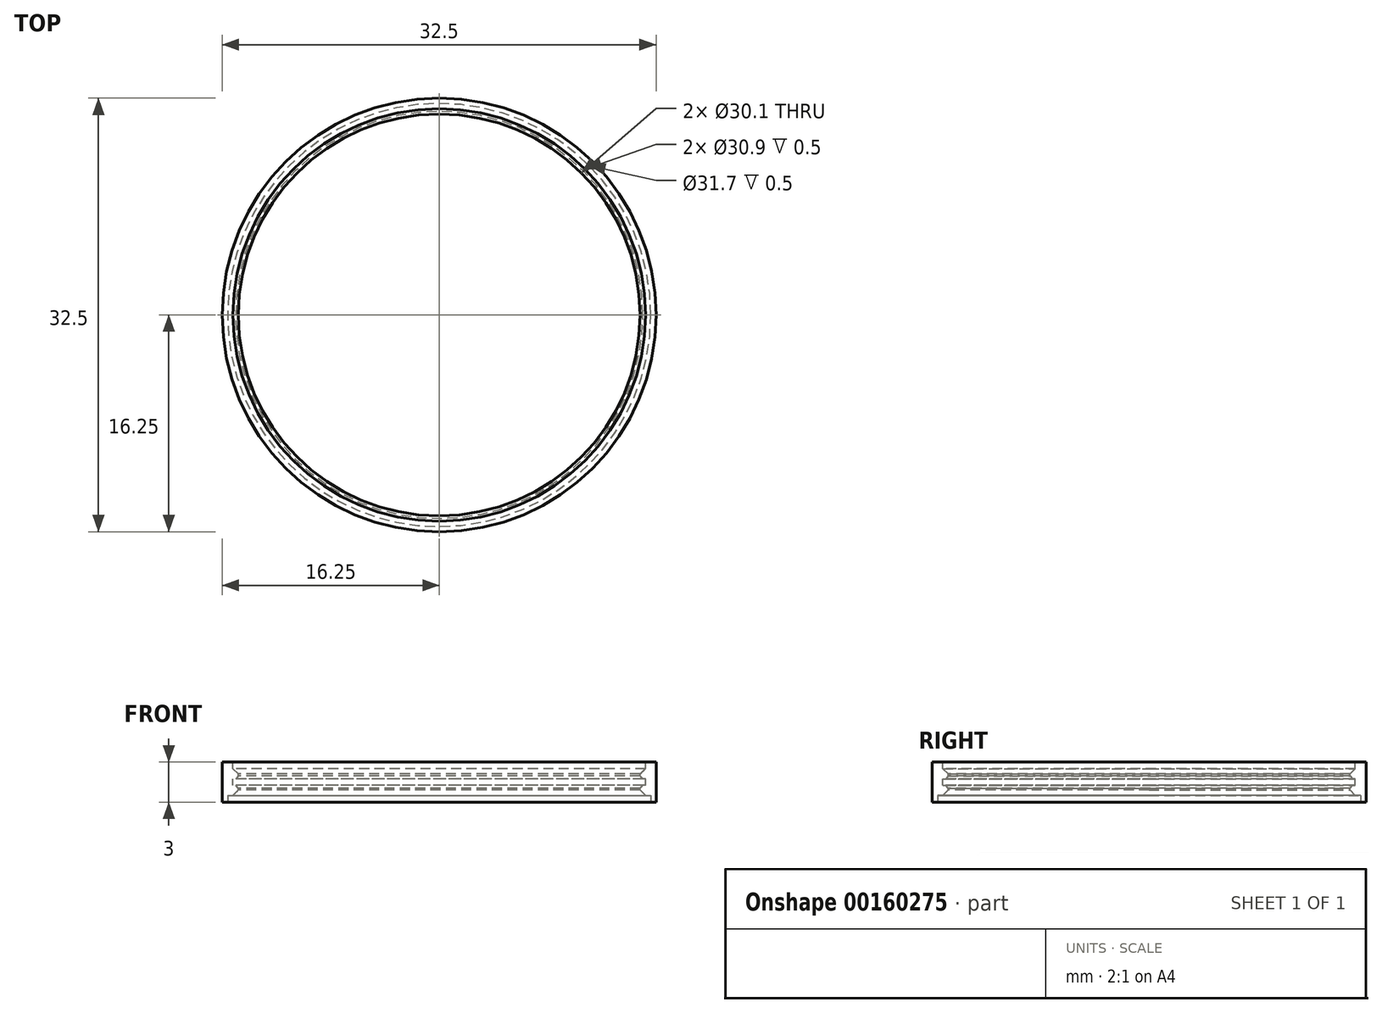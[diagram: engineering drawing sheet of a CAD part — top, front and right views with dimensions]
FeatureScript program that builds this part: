
annotation { "Feature Type Name" : "Feature", "Feature Type Description" : "" }
export const myFeature = defineFeature(function(context is Context, id is Id, definition is map)
    precondition{}
    {
        {
            var Q0;
            Q0=qCreatedBy(makeId("Top.planeOp"),FACE);
            var sketch = newSketch(context, id + "F0", { "sketchPlane" : qUnion([Q0])});
            skCircle(sketch, "E0", {"center": v(0, 0) * mm, "radius": 16.25 * mm});
            skSolve(sketch);
        }
        {
            var Q0;
            Q0=qSketchRegion(id+"F0",true);
            extrude(context, id + "F1", {"entities" : qUnion([Q0]), "endBound" : BoundingType.SYMMETRIC, "depth" : 3 * mm});
        }
        {
            var Q0;
            Q0=makeQuery(id+"F1.opExtrude","CAP_FACE",FACE,{"disambiguationData":[OSD([sQuery(id+"F0.wireOp",EDGE,"E0")])],"isStart":false});
            var sketch = newSketch(context, id + "F2", { "sketchPlane" : qUnion([Q0])});
            skCircle(sketch, "E1", {"center": v(0, 0) * mm, "radius": 15.05 * mm});
            skSolve(sketch);
        }
        {
            var Q0;
            Q0=qSketchRegion(id+"F2",true);
            extrude(context, id + "F3", {"entities" : qUnion([Q0]), "operationType" : NewBodyOperationType.REMOVE, "endBound" : BoundingType.THROUGH_ALL, "oppositeDirection" : true, "depth" : 25 * mm});
        }
        {
            var Q0;
            Q0=qCreatedBy(makeId("Top.planeOp"),FACE);
            var sketch = newSketch(context, id + "F4", { "sketchPlane" : qUnion([Q0])});
            skCircle(sketch, "E2", {"center": v(0, 0) * mm, "radius": 15.45 * mm});
            skSolve(sketch);
        }
        {
            var Q0;
            Q0 = qSketchRegion(id + "F4", true);
            extrude(context, id + "F5", {"entities" : qUnion([Q0]), "operationType" : NewBodyOperationType.REMOVE, "endBound" : BoundingType.SYMMETRIC, "oppositeDirection" : true, "depth" : 0.5 * mm});
        }
        {
            var Q0;
            Q0=makeQuery(id+"F5.boolean.opBoolean","INTERSECT",EDGE,{"derivedFrom":[makeQuery(id+"F3.boolean.opBoolean","COPY",FACE,{"derivedFrom":makeQuery(id+"F3.opExtrude","SWEPT_FACE",FACE,{"disambiguationData":[OSD([sQuery(id+"F2.wireOp",EDGE,"E1")])]})}),makeQuery(id+"F5.opExtrude","CAP_FACE",FACE,{"disambiguationData":[OSD([sQuery(id+"F4.wireOp",EDGE,"E2")])],"isStart":true})]});
            var Q1;
            Q1=makeQuery(id+"F5.boolean.opBoolean","INTERSECT",EDGE,{"derivedFrom":[makeQuery(id+"F3.boolean.opBoolean","COPY",FACE,{"derivedFrom":makeQuery(id+"F3.opExtrude","SWEPT_FACE",FACE,{"disambiguationData":[OSD([sQuery(id+"F2.wireOp",EDGE,"E1")])]})}),makeQuery(id+"F5.opExtrude","CAP_FACE",FACE,{"disambiguationData":[OSD([sQuery(id+"F4.wireOp",EDGE,"E2")])],"isStart":false})]});
            chamfer(context, id + "F6", {"entities" : qUnion([Q0, Q1]), "width" : 0.2 * mm, "tangentPropagation" : true});
        }
        {
            var Q0;
            Q0=makeQuery(id+"F1.opExtrude","CAP_FACE",FACE,{"disambiguationData":[OSD([sQuery(id+"F0.wireOp",EDGE,"E0")])],"isStart":false});
            var sketch = newSketch(context, id + "F7", { "sketchPlane" : qUnion([Q0])});
            skCircle(sketch, "E3", {"center": v(0, 0) * mm, "radius": 15.45 * mm});
            skSolve(sketch);
        }
        {
            var Q0;
            Q0 = qSketchRegion(id + "F7", true);
            extrude(context, id + "F8", {"entities" : qUnion([Q0]), "operationType" : NewBodyOperationType.REMOVE, "oppositeDirection" : true, "depth" : 0.5 * mm});
        }
        {
            var Q0;
            Q0=makeQuery(id+"F1.opExtrude","CAP_FACE",FACE,{"disambiguationData":[OSD([sQuery(id+"F0.wireOp",EDGE,"E0")])],"isStart":true});
            var sketch = newSketch(context, id + "F9", { "sketchPlane" : qUnion([Q0])});
            skCircle(sketch, "E4", {"center": v(0, 0) * mm, "radius": 15.85 * mm});
            skSolve(sketch);
        }
        {
            var Q0;
            Q0 = qSketchRegion(id + "F9", true);
            extrude(context, id + "F10", {"entities" : qUnion([Q0]), "operationType" : NewBodyOperationType.REMOVE, "oppositeDirection" : true, "depth" : .5 * mm});
        }
        {
            var Q0;
            Q0=makeQuery(id+"F8.boolean.opBoolean","INTERSECT",EDGE,{"derivedFrom":[makeQuery(id+"F5.boolean.opBoolean","SPLIT",FACE,{"disambiguationData":[TD([makeQuery(id+"F1.opExtrude","CAP_FACE",FACE,{"disambiguationData":[OSD([sQuery(id+"F0.wireOp",EDGE,"E0")])],"isStart":false})])],"derivedFrom":makeQuery(id+"F3.boolean.opBoolean","COPY",FACE,{"derivedFrom":makeQuery(id+"F3.opExtrude","SWEPT_FACE",FACE,{"disambiguationData":[OSD([sQuery(id+"F2.wireOp",EDGE,"E1")])]})})}),makeQuery(id+"F8.opExtrude","CAP_FACE",FACE,{"disambiguationData":[OSD([sQuery(id+"F7.wireOp",EDGE,"E3")])],"isStart":false})]});
            var Q1;
            Q1=makeQuery(id+"F10.boolean.opBoolean","INTERSECT",EDGE,{"derivedFrom":[makeQuery(id+"F5.boolean.opBoolean","SPLIT",FACE,{"disambiguationData":[TD([makeQuery(id+"F1.opExtrude","CAP_FACE",FACE,{"disambiguationData":[OSD([sQuery(id+"F0.wireOp",EDGE,"E0")])],"isStart":true})])],"derivedFrom":makeQuery(id+"F3.boolean.opBoolean","COPY",FACE,{"derivedFrom":makeQuery(id+"F3.opExtrude","SWEPT_FACE",FACE,{"disambiguationData":[OSD([sQuery(id+"F2.wireOp",EDGE,"E1")])]})})}),makeQuery(id+"F10.opExtrude","CAP_FACE",FACE,{"disambiguationData":[OSD([sQuery(id+"F9.wireOp",EDGE,"E4")])],"isStart":false})]});
            chamfer(context, id + "F11", {"entities" : qUnion([Q0, Q1]), "width" : 0.4 * mm, "tangentPropagation" : true});
        }
    });
